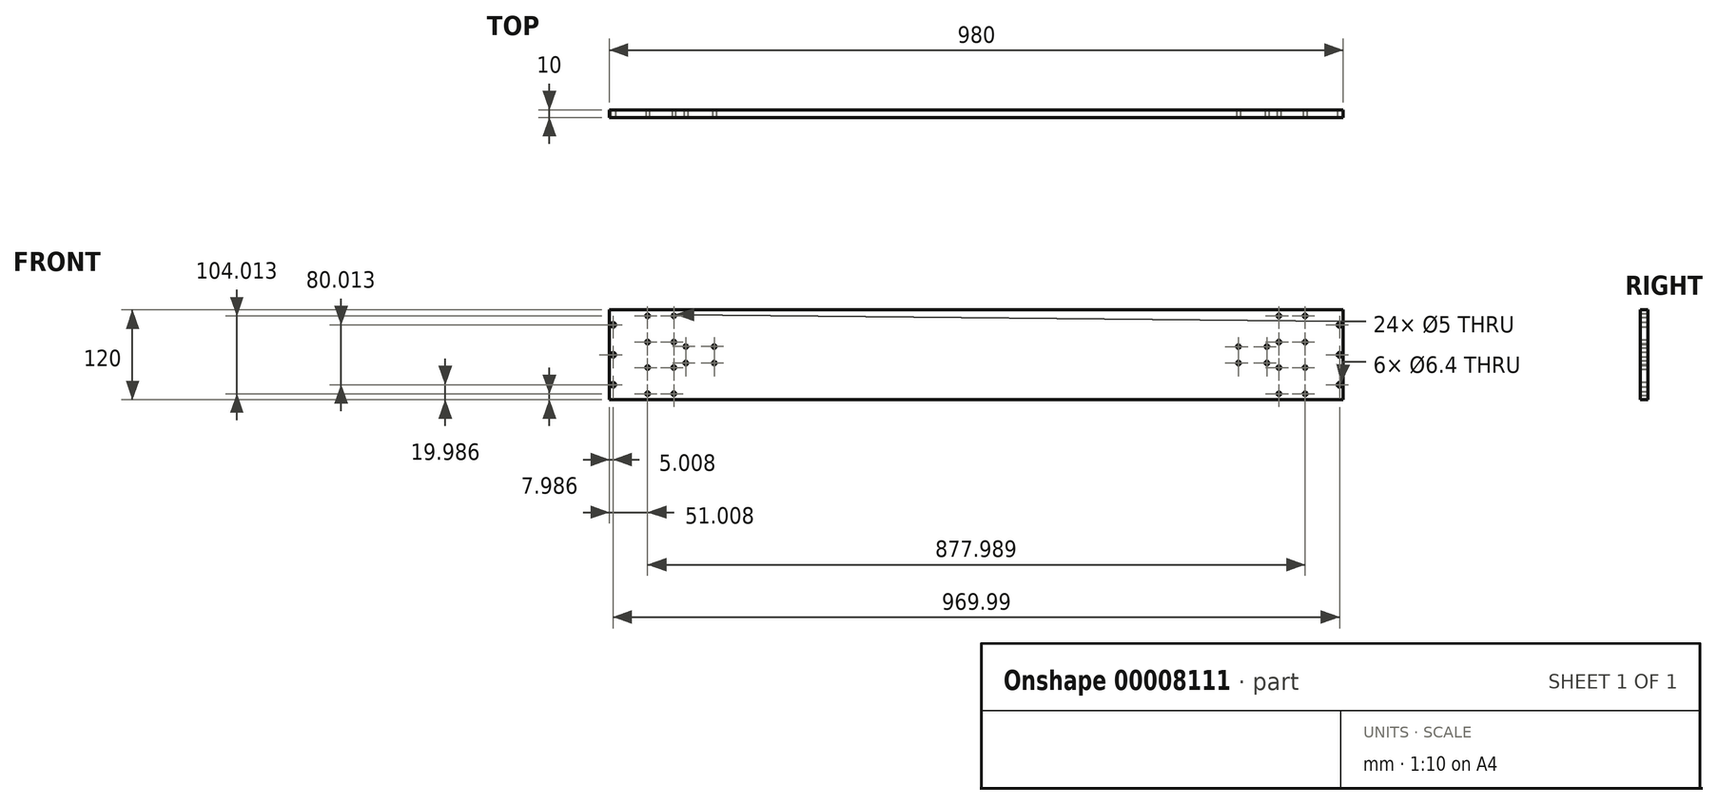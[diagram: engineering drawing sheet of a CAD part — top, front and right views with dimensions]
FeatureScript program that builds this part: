
annotation { "Feature Type Name" : "Feature", "Feature Type Description" : "" }
export const myFeature = defineFeature(function(context is Context, id is Id, definition is map)
    precondition{}
    {
        {
            var Q0;
            Q0=qCreatedBy(makeId("Front.planeOp"),FACE);
            var sketch = newSketch(context, id + "F0", { "sketchPlane" : qUnion([Q0])});
            skLineSegment(sketch, "E0", {"start": v(-457.54, -32.51) * mm, "end": v(522.46, -32.51) * mm});
            skLineSegment(sketch, "E1", {"start": v(522.46, -32.51) * mm, "end": v(522.46, 87.49) * mm});
            skLineSegment(sketch, "E2", {"start": v(522.46, 87.49) * mm, "end": v(-457.54, 87.49) * mm});
            skLineSegment(sketch, "E3", {"start": v(-457.54, 87.49) * mm, "end": v(-457.54, -32.51) * mm});
            skCircle(sketch, "E4", {"center": v(-406.53, 79.49) * mm, "radius": 2.5 * mm});
            skCircle(sketch, "E5", {"center": v(-371.53, 79.49) * mm, "radius": 2.5 * mm});
            skCircle(sketch, "E6", {"center": v(-371.53, 44.49) * mm, "radius": 2.5 * mm});
            skCircle(sketch, "E7", {"center": v(-406.53, 44.49) * mm, "radius": 2.5 * mm});
            skCircle(sketch, "E8", {"center": v(-406.53, 10.49) * mm, "radius": 2.5 * mm});
            skCircle(sketch, "E9", {"center": v(-371.53, 10.49) * mm, "radius": 2.5 * mm});
            skCircle(sketch, "E10", {"center": v(-406.53, -24.51) * mm, "radius": 2.5 * mm});
            skCircle(sketch, "E11", {"center": v(-371.53, -24.51) * mm, "radius": 2.5 * mm});
            skCircle(sketch, "E12", {"center": v(-452.53, 67.49) * mm, "radius": 3.2 * mm});
            skCircle(sketch, "E13", {"center": v(-452.53, 27.49) * mm, "radius": 3.2 * mm});
            skCircle(sketch, "E14", {"center": v(-452.53, -12.51) * mm, "radius": 3.2 * mm});
            skCircle(sketch, "E15", {"center": v(-355.53, 38.49) * mm, "radius": 2.5 * mm});
            skCircle(sketch, "E16", {"center": v(-317.53, 38.49) * mm, "radius": 2.5 * mm});
            skCircle(sketch, "E17", {"center": v(-317.53, 16.49) * mm, "radius": 2.5 * mm});
            skCircle(sketch, "E18", {"center": v(-355.53, 16.49) * mm, "radius": 2.5 * mm});
            skCircle(sketch, "E19.0.MirrorC", {"center": v(436.46, 10.48) * mm, "radius": 2.5 * mm});
            skCircle(sketch, "E19.1.MirrorC", {"center": v(382.46, 38.48) * mm, "radius": 2.5 * mm});
            skCircle(sketch, "E19.2.MirrorC", {"center": v(471.46, -24.52) * mm, "radius": 2.5 * mm});
            skCircle(sketch, "E19.3.MirrorC", {"center": v(471.46, 10.48) * mm, "radius": 2.5 * mm});
            skCircle(sketch, "E19.4.MirrorC", {"center": v(436.46, -24.52) * mm, "radius": 2.5 * mm});
            skCircle(sketch, "E19.5.MirrorC", {"center": v(517.46, 67.48) * mm, "radius": 3.2 * mm});
            skCircle(sketch, "E19.6.MirrorC", {"center": v(382.46, 16.48) * mm, "radius": 2.5 * mm});
            skCircle(sketch, "E19.7.MirrorC", {"center": v(436.46, 79.48) * mm, "radius": 2.5 * mm});
            skCircle(sketch, "E19.8.MirrorC", {"center": v(471.46, 79.48) * mm, "radius": 2.5 * mm});
            skCircle(sketch, "E19.9.MirrorC", {"center": v(517.46, 27.48) * mm, "radius": 3.2 * mm});
            skCircle(sketch, "E19.10.MirrorC", {"center": v(420.46, 38.48) * mm, "radius": 2.5 * mm});
            skCircle(sketch, "E19.11.MirrorC", {"center": v(517.46, -12.52) * mm, "radius": 3.2 * mm});
            skCircle(sketch, "E19.12.MirrorC", {"center": v(420.46, 16.48) * mm, "radius": 2.5 * mm});
            skCircle(sketch, "E19.13.MirrorC", {"center": v(471.46, 44.48) * mm, "radius": 2.5 * mm});
            skCircle(sketch, "E19.14.MirrorC", {"center": v(436.46, 44.48) * mm, "radius": 2.5 * mm});
            skSolve(sketch);
        }
        {
            var Q0;
            Q0=makeQuery(id+"F0.imprint","IMPRINT",FACE,{"disambiguationData":[TD([[makeQuery(id+"F0.imprint","IMPRINT",EDGE,{"derivedFrom":sQuery(id+"F0.wireOp",EDGE,"E0")}),1.0]])]});
            extrude(context, id + "F1", {"entities" : qUnion([Q0]), "oppositeDirection" : true, "depth" : 10 * mm});
        }
    });
